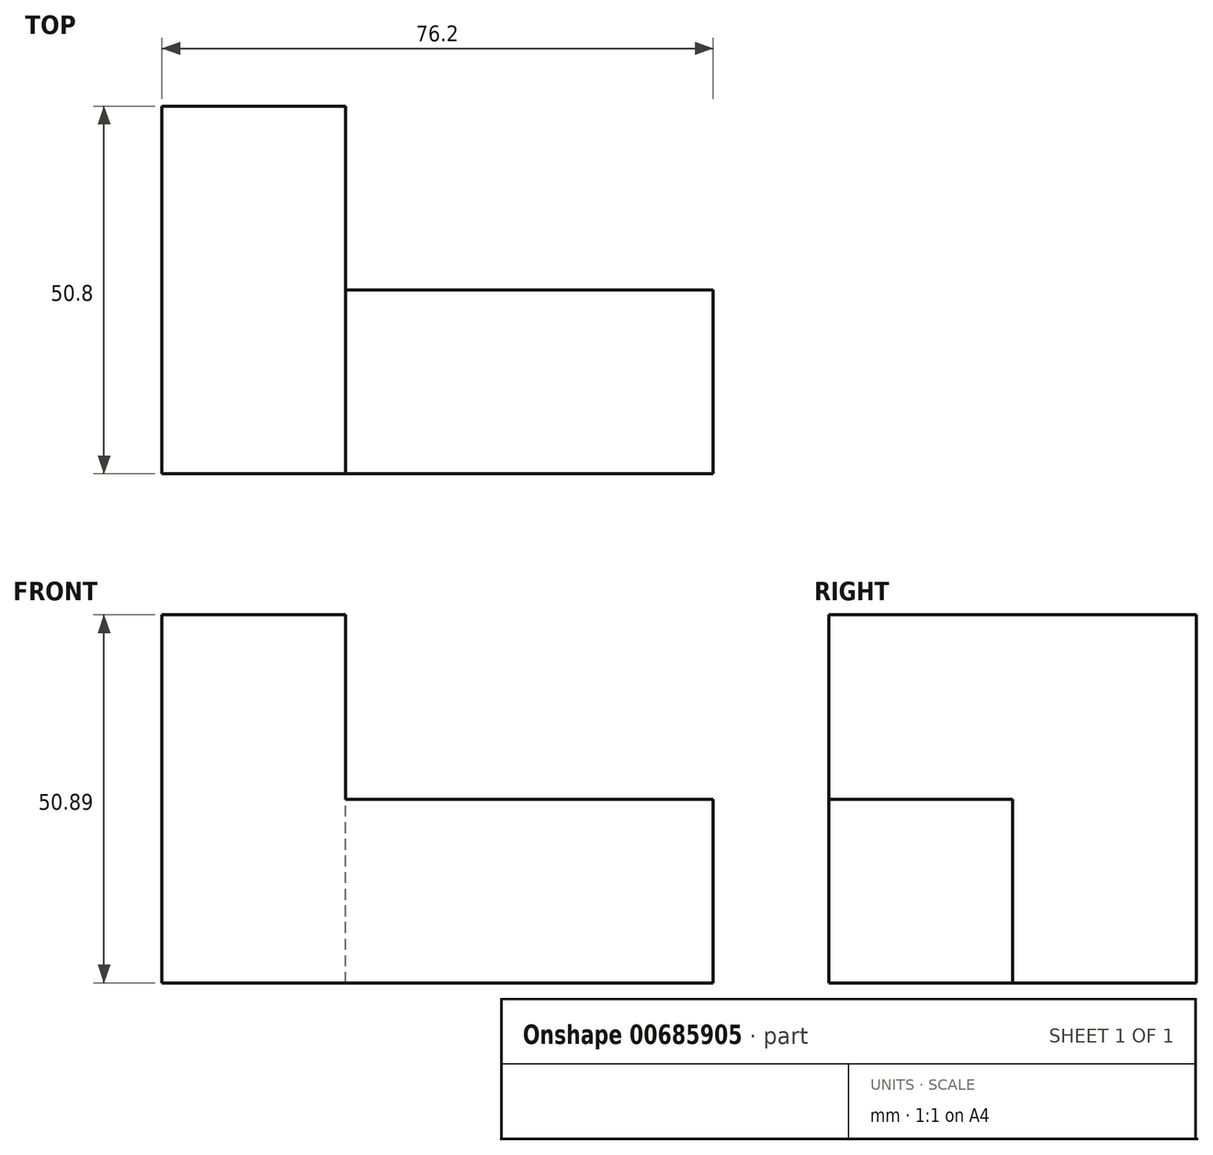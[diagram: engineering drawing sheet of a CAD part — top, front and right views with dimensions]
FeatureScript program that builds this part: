
annotation { "Feature Type Name" : "Feature", "Feature Type Description" : "" }
export const myFeature = defineFeature(function(context is Context, id is Id, definition is map)
    precondition{}
    {
        {
            var Q0;
            Q0=qCreatedBy(makeId("Front.planeOp"),FACE);
            var sketch = newSketch(context, id + "F0", { "sketchPlane" : qUnion([Q0])});
            skLineSegment(sketch, "E0", {"start": v(0, 0) * mm, "end": v(0, 50.89) * mm});
            skLineSegment(sketch, "E1", {"start": v(0, 50.89) * mm, "end": v(25.4, 50.89) * mm});
            skLineSegment(sketch, "E2", {"start": v(25.4, 50.89) * mm, "end": v(25.4, 0) * mm});
            skLineSegment(sketch, "E3", {"start": v(25.4, 0) * mm, "end": v(0, 0) * mm});
            skSolve(sketch);
        }
        {
            var Q0;
            Q0 = qSketchRegion(id + "F0", true);
            extrude(context, id + "F1", {"entities" : qUnion([Q0]), "depth" : 50.8 * mm, "offsetDistance" : 25.4 * mm});
        }
        {
            var Q0;
            Q0=makeQuery(id+"F1.opExtrude","SWEPT_FACE",FACE,{"disambiguationData":[OSD([sQuery(id+"F0.wireOp",EDGE,"E2")])]});
            var sketch = newSketch(context, id + "F2", { "sketchPlane" : qUnion([Q0])});
            skLineSegment(sketch, "E4.bottom", {"start": v(-50.8, 0) * mm, "end": v(-25.4, 0) * mm});
            skLineSegment(sketch, "E4.top", {"start": v(-50.8, 25.4) * mm, "end": v(-25.4, 25.4) * mm});
            skLineSegment(sketch, "E4.left", {"start": v(-50.8, 0) * mm, "end": v(-50.8, 25.4) * mm});
            skLineSegment(sketch, "E4.right", {"start": v(-25.4, 0) * mm, "end": v(-25.4, 25.4) * mm});
            skSolve(sketch);
        }
        {
            var Q0;
            Q0=makeQuery(id+"F2.imprint","IMPRINT",FACE,{"disambiguationData":[TD([[makeQuery(id+"F2.imprint","IMPRINT",EDGE,{"derivedFrom":sQuery(id+"F2.wireOp",EDGE,"E4.bottom")}),1.0]])]});
            extrude(context, id + "F3", {"entities" : qUnion([Q0]), "operationType" : NewBodyOperationType.ADD, "depth" : 50.8 * mm, "offsetDistance" : 25.4 * mm});
        }
    });
